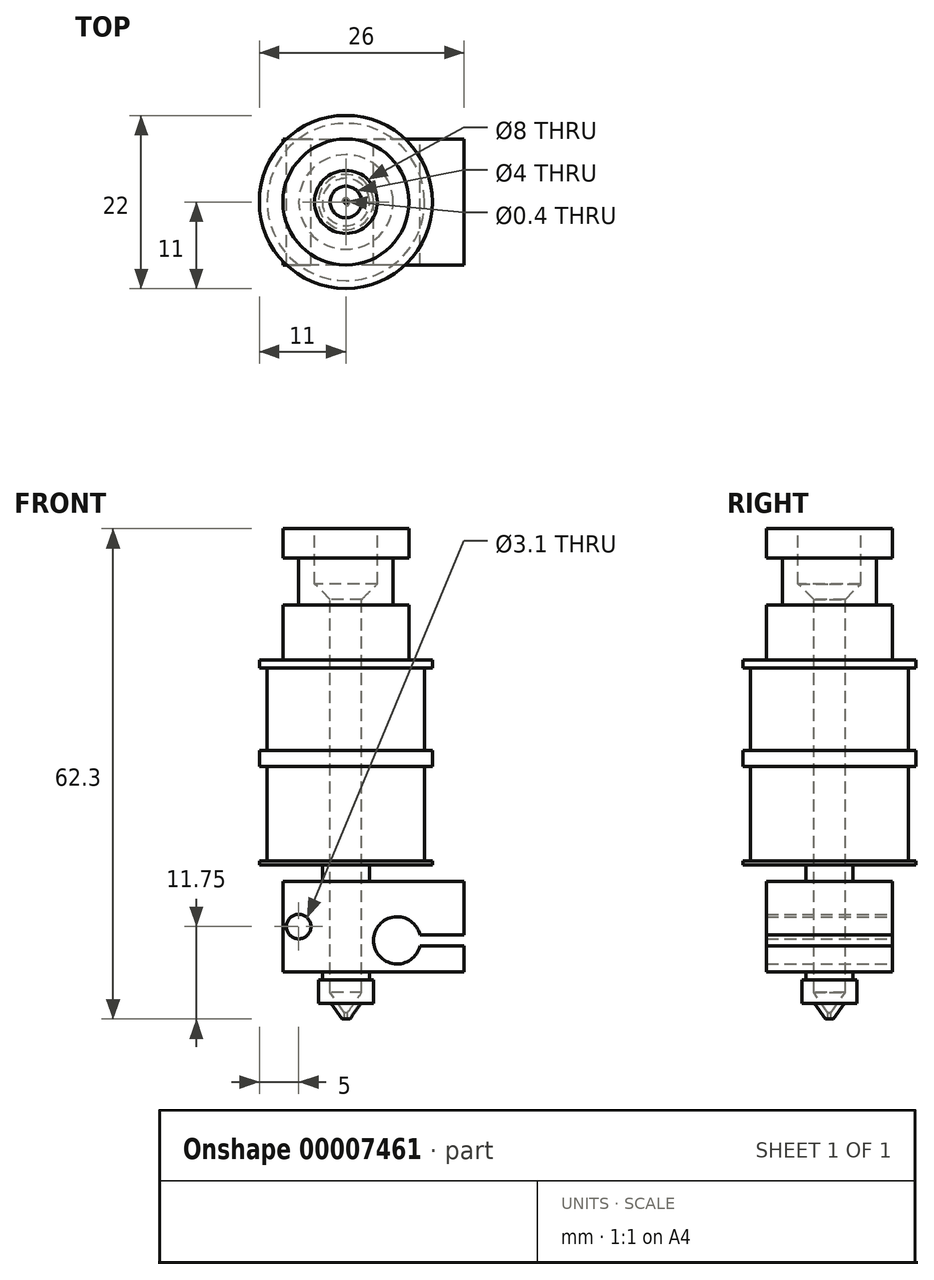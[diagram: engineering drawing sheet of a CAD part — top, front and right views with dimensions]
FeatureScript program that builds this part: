
annotation { "Feature Type Name" : "Feature", "Feature Type Description" : "" }
export const myFeature = defineFeature(function(context is Context, id is Id, definition is map)
    precondition{}
    {
        {
            var Q0;
            Q0=qCreatedBy(makeId("Front.planeOp"),FACE);
            var sketch = newSketch(context, id + "F0", { "sketchPlane" : qUnion([Q0])});
            skLineSegment(sketch, "E0", {"start": v(0, 0) * mm, "end": v(8, 0) * mm});
            skLineSegment(sketch, "E1", {"start": v(8, 0) * mm, "end": v(8, -3.7) * mm});
            skLineSegment(sketch, "E2", {"start": v(8, -3.7) * mm, "end": v(6, -3.7) * mm});
            skLineSegment(sketch, "E3", {"start": v(6, -3.7) * mm, "end": v(6, -9.7) * mm});
            skLineSegment(sketch, "E4", {"start": v(6, -9.7) * mm, "end": v(8, -9.7) * mm});
            skLineSegment(sketch, "E5", {"start": v(8, -9.7) * mm, "end": v(8, -16.7) * mm});
            skLineSegment(sketch, "E6", {"start": v(8, -16.7) * mm, "end": v(11, -16.7) * mm});
            skLineSegment(sketch, "E7", {"start": v(11, -16.7) * mm, "end": v(11, -17.7) * mm});
            skLineSegment(sketch, "E8", {"start": v(11, -17.7) * mm, "end": v(10, -17.7) * mm});
            skLineSegment(sketch, "E9", {"start": v(10, -17.7) * mm, "end": v(10, -28.2) * mm});
            skLineSegment(sketch, "E10", {"start": v(10, -28.2) * mm, "end": v(11, -28.2) * mm});
            skLineSegment(sketch, "E11", {"start": v(11, -28.2) * mm, "end": v(11, -30.2) * mm});
            skLineSegment(sketch, "E12", {"start": v(11, -30.2) * mm, "end": v(10, -30.2) * mm});
            skLineSegment(sketch, "E13", {"start": v(10, -30.2) * mm, "end": v(10, -42.2) * mm});
            skLineSegment(sketch, "E14", {"start": v(10, -42.2) * mm, "end": v(11, -42.2) * mm});
            skLineSegment(sketch, "E15", {"start": v(11, -42.2) * mm, "end": v(11, -42.7) * mm});
            skLineSegment(sketch, "E16", {"start": v(11, -42.7) * mm, "end": v(3, -42.7) * mm});
            skLineSegment(sketch, "E17", {"start": v(3, -57.3) * mm, "end": v(3.5, -57.3) * mm});
            skLineSegment(sketch, "E18", {"start": v(3.5, -57.3) * mm, "end": v(3.5, -60.3) * mm});
            skLineSegment(sketch, "E19", {"start": v(3.5, -60.3) * mm, "end": v(1.9, -60.3) * mm});
            skLineSegment(sketch, "E20", {"start": v(8, -9.7) * mm, "end": v(8, -3.7) * mm, "construction": true});
            skLineSegment(sketch, "E21", {"start": v(11, -17.7) * mm, "end": v(11, -28.2) * mm, "construction": true});
            skLineSegment(sketch, "E22", {"start": v(11, -30.2) * mm, "end": v(11, -42.2) * mm, "construction": true});
            skLineSegment(sketch, "E23", {"start": v(4, 0) * mm, "end": v(4, -7) * mm});
            skLineSegment(sketch, "E24", {"start": v(4, -7) * mm, "end": v(2, -9) * mm});
            skLineSegment(sketch, "E25", {"start": v(2, -9) * mm, "end": v(2, -58.93) * mm});
            skLineSegment(sketch, "E26", {"start": v(2, -58.93) * mm, "end": v(0.2, -61.5) * mm});
            skLineSegment(sketch, "E27", {"start": v(0.2, -61.5) * mm, "end": v(0.2, -62.3) * mm});
            skLineSegment(sketch, "E28", {"start": v(0.2, -62.3) * mm, "end": v(0.5, -62.3) * mm});
            skLineSegment(sketch, "E29", {"start": v(0.5, -62.3) * mm, "end": v(1.9, -60.3) * mm});
            skLineSegment(sketch, "E30", {"start": v(10, -28.2) * mm, "end": v(10, -30.2) * mm, "construction": true});
            skLineSegment(sketch, "E31", {"start": v(3, -42.7) * mm, "end": v(3, -49.8) * mm});
            skLineSegment(sketch, "E32", {"start": v(3, -49.8) * mm, "end": v(3, -57.3) * mm});
            skLineSegment(sketch, "E33", {"start": v(0, 0) * mm, "end": v(0, -84) * mm});
            skSolve(sketch);
        }
        {
            var Q0;
            {var subQ2=sQuery(id+"F0.wireOp",EDGE,"E1");Q0=makeQuery(id+"F0.imprint","IMPRINT",FACE,{"disambiguationData":[TD([[makeQuery(id+"F0.imprint","IMPRINT",EDGE,{"derivedFrom":subQ2}),-1.0]])]});}
            var Q1;
            Q1=sQuery(id+"F0.wireOp",EDGE,"E33");
            revolve(context, id + "F1", {"entities" : qUnion([Q0]), "axis" : qUnion([Q1]), "revolveType" : RevolveType.FULL});
        }
        {
            var Q0;
            Q0=qCreatedBy(makeId("Top.planeOp"),FACE);
            cPlane(context, id + "F2", {"entities" : qUnion([Q0]), "cplaneType" : CPlaneType.OFFSET, "offset" : 44.8 * mm, "oppositeDirection" : true, "width" : 150 * mm, "height" : 150 * mm});
        }
        {
            var Q0;
            Q0=qCreatedBy(id+"F2.planeOp",FACE);
            var sketch = newSketch(context, id + "F3", { "sketchPlane" : qUnion([Q0])});
            skCircle(sketch, "E34", {"center": v(0, 0) * mm, "radius": 3 * mm});
            skLineSegment(sketch, "E35", {"start": v(-8, 8) * mm, "end": v(15, 8) * mm});
            skLineSegment(sketch, "E36", {"start": v(15, 8) * mm, "end": v(15, -8) * mm});
            skLineSegment(sketch, "E37", {"start": v(15, -8) * mm, "end": v(-8, -8) * mm});
            skLineSegment(sketch, "E38", {"start": v(-8, -8) * mm, "end": v(-8, 8) * mm});
            skLineSegment(sketch, "E39", {"start": v(0, 0) * mm, "end": v(-8, 0) * mm, "construction": true});
            skSolve(sketch);
        }
        {
            var Q0;
            Q0=makeQuery(id+"F3.imprint","IMPRINT",FACE,{"disambiguationData":[TD([[makeQuery(id+"F3.imprint","IMPRINT",EDGE,{"derivedFrom":sQuery(id+"F3.wireOp",EDGE,"E34")}),-1.0]])]});
            extrude(context, id + "F4", {"entities" : qUnion([Q0]), "operationType" : NewBodyOperationType.ADD, "oppositeDirection" : true, "depth" : 11.5 * mm});
        }
        {
            var Q0;
            Q0=makeQuery(id+"F4.opExtrude","SWEPT_FACE",FACE,{"disambiguationData":[OSD([sQuery(id+"F3.wireOp",EDGE,"E35")])]});
            var sketch = newSketch(context, id + "F5", { "sketchPlane" : qUnion([Q0])});
            skLineSegment(sketch, "E40.0.0", {"start": v(8, -44.8) * mm, "end": v(-15, -44.8) * mm, "construction": true});
            skLineSegment(sketch, "E40.0.1", {"start": v(-15, -44.8) * mm, "end": v(-15, -56.3) * mm, "construction": true});
            skLineSegment(sketch, "E40.0.2", {"start": v(-15, -56.3) * mm, "end": v(8, -56.3) * mm, "construction": true});
            skLineSegment(sketch, "E40.0.3", {"start": v(8, -56.3) * mm, "end": v(8, -44.8) * mm, "construction": true});
            skCircle(sketch, "E41", {"center": v(-6.5, -52.3) * mm, "radius": 3 * mm});
            skCircle(sketch, "E42", {"center": v(6, -50.55) * mm, "radius": 1.55 * mm});
            skLineSegment(sketch, "E43", {"start": v(-9.42, -51.6) * mm, "end": v(-15, -51.6) * mm});
            skLineSegment(sketch, "E44", {"start": v(-15, -51.6) * mm, "end": v(-15, -53) * mm});
            skLineSegment(sketch, "E45", {"start": v(-15, -53) * mm, "end": v(-9.42, -53) * mm});
            skSolve(sketch);
        }
        {
            var Q0;
            Q0 = qSketchRegion(id + "F5", true);
            extrude(context, id + "F6", {"entities" : qUnion([Q0]), "operationType" : NewBodyOperationType.REMOVE, "endBound" : BoundingType.THROUGH_ALL, "oppositeDirection" : true, "depth" : 25 * mm});
        }
    });
